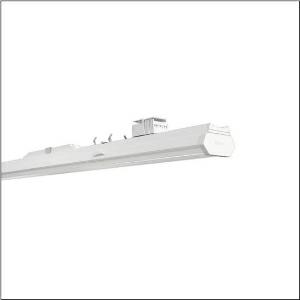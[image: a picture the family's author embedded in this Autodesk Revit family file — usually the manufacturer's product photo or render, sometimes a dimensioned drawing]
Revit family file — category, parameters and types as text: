
# Revit family: licross_r__11_protected_tw_51td1btnt8xx_5d1b
name_source: partatom
category: Lighting Fixtures
units: mm (PartAtom-declared; Revit-internal decimal feet)

## family parameters
Cut with Voids When Loaded = No
Host = Face
Light Source = No
Part Type = Normal
Room Calculation Point = No
Round Connector Dimension = Use Diameter
Shared = No

## types (1)
- --- (1 x LED 2700 K ... 6500 K, 8450 lm, 56 W, 2700K)
    Apparent Load = 56 VA
    CIE Flux Codes = 54 82 95 97 100
    Color Rendering = 80
    Color Temperature = 2700K
    Default Elevation = 1800 mm
    Description = Licross® 11 Protected TW, luminaire insert, of sheet steel, galvanised, coil coated, white, length: 1.500mm, width: 90mm, height: 101mm, LED rated luminous flux: 8.450lm, light colour: 8tw, control gear: DALI DT8, with plug, 5-pole, with phase selection, mains connection: 220..240V, AC, 50/60Hz, rated input power: 56W, halogen-free wiring, primary optical cover: cover, of PMMA, light emission: direct distribution, primary light characteristic: symmetric, protection rating (complete): IP54, insulation class (complete): insulation class I (protective earthing), certification: CE, ENEC, VDE, UKCA, protection symbol: D if used in an environment with non-conductive dust loads with corresponding accessories, impact resistance: IK06, permissible ambient temperature for indoor applications: -25..+35°C, corresponds to IFS (International Featured Standards) requirements for safety and quality in the food industry, reducing of maximum allowable ambient temperature of 5°C with ceiling mounting, LABS conformity tested according to VDMA 24364:2018-05, packaging unit: 1 piece
    Height = 92 mm
    Lamp = 1 x LED 2700 K ... 6500 K
    Lamp Light Flux = 8450 lm
    Lamp Power = 56 W
    Lamp count = 1
    Length = 1500 mm
    Luminous efficacy = 151 lm/W
    Manufacturer = Siteco
    ModVariant = No
    Model = 51TD1BTNT8XX
    Mounting Place = Ceiling
    Mounting Type = Pendant
    Number of Poles = 1
    OnlyDefault = Yes
    Power Factor = 1
    Product Name = Licross® 11 Protected TW
    Product group = luminaire insert
    ProductGroupID = 902
    Protection Class = Protection class I
    Protection Degree = IP 54
    RLX_Detail_Level = 1
    RLX_Emergency_Light_Flux = 0 lm
    RLX_Emergency_Type = 0
    RLX_Emergency_Type_DB = No
    RlxData = <blob elided: 20661 chars, md5=8811ded2>
    Socket = socket
    Standby Power = 0 W
    System Light Flux = 8450 lm
    System Power = 56 W
    Type Comments = individual setting: CCT=2700K
    Type Image = l_1256145.jpg
    URL = http://relux.com
    VarID = @adj_049262
    Voltage = 0 V
    Weight = 0.00 kg
    Width = 88 mm

## geometry (parser evidence)
native form markers: Blend x4, Sweep x12
no freeform markers — native parametric forms only
